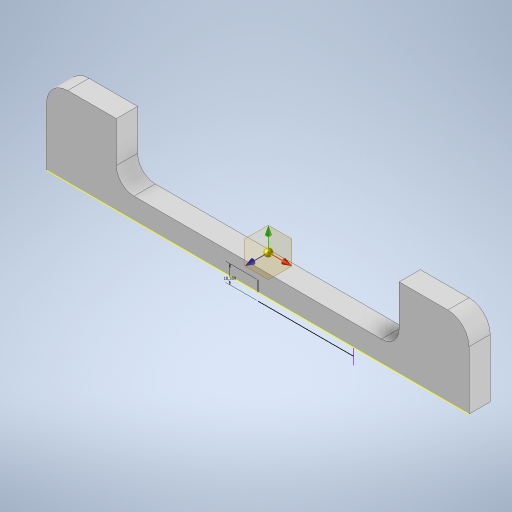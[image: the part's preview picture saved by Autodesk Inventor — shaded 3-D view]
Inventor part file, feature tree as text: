
AUTODESK INVENTOR PART (.ipt)
format: ipt  version: 2024 (Build 280153000, 153)  size: 252,416 bytes
history: native  units: mm
features: other x5, sketch x1
ambient origin geometry x8: Origin, YZ Plane, XZ Plane, XY Plane, X Axis, Y Axis, Z Axis, Center Point
bodies: Body1 (feature_tree)
feature tree (6):
  other  "FRONTAL_1"
  other  "Generador_de_Piezas.ipt"
  other  "Desplazar cuerpo1"
  sketch  "Boceto1"  dims[d0=10.0mm d1=-726.851mm d2=-2373.08mm d3=0.0mm d4=10.35894mm]
  other  "FRONTAL_1::Generador_de_Piezas.ipt"
  other  "OperaciónIdentificador1"
